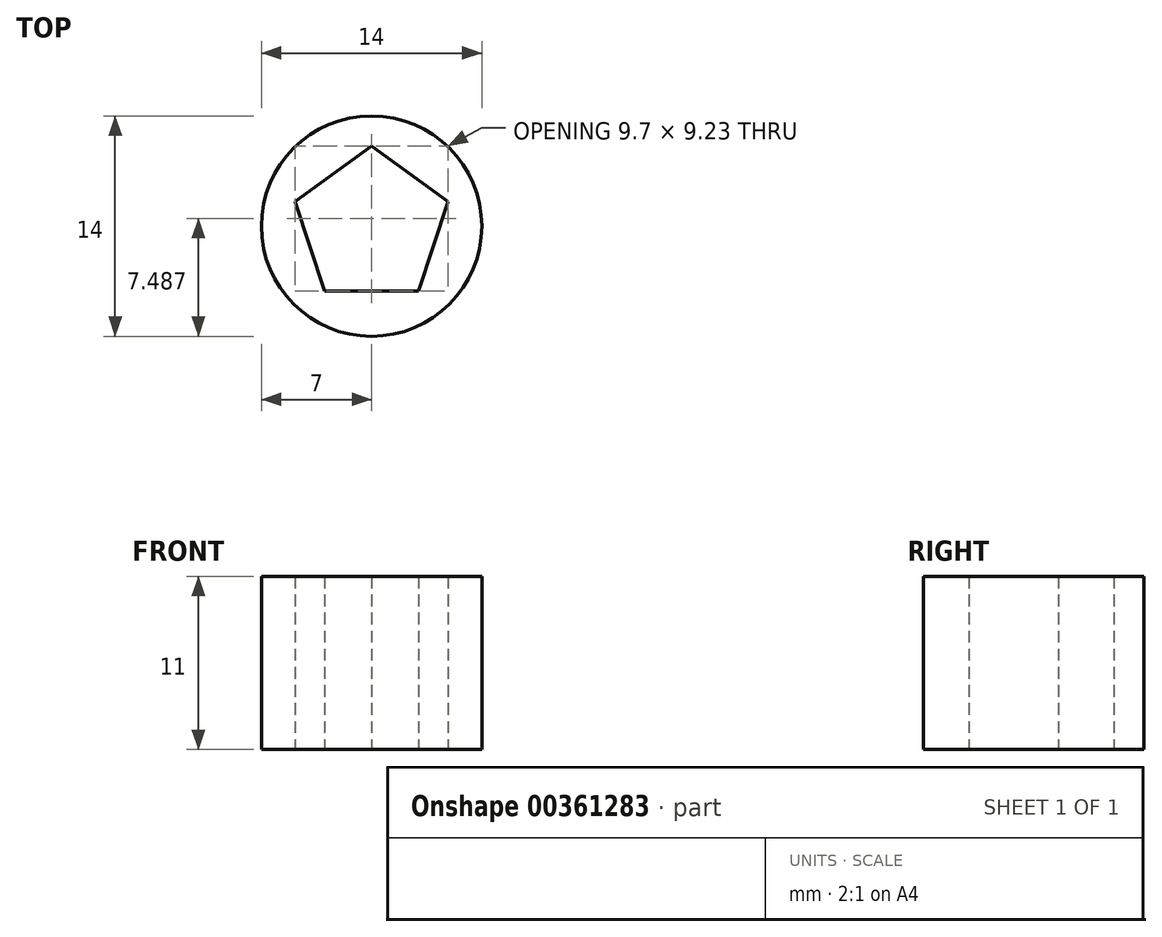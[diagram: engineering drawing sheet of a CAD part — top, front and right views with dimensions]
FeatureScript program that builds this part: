
annotation { "Feature Type Name" : "Feature", "Feature Type Description" : "" }
export const myFeature = defineFeature(function(context is Context, id is Id, definition is map)
    precondition{}
    {
        {
            var Q0;
            Q0=qCreatedBy(makeId("Top.planeOp"),FACE);
            var sketch = newSketch(context, id + "F0", { "sketchPlane" : qUnion([Q0])});
            skCircle(sketch, "E0.cCircle", {"center": v(0, 0) * mm, "radius": 4.13 * mm, "construction": true});
            skLineSegment(sketch, "E0.0", {"start": v(4.85, 1.58) * mm, "end": v(3, -4.13) * mm});
            skLineSegment(sketch, "E0.1", {"start": v(3, -4.13) * mm, "end": v(-3, -4.13) * mm});
            skLineSegment(sketch, "E0.2", {"start": v(-3, -4.13) * mm, "end": v(-4.85, 1.58) * mm});
            skLineSegment(sketch, "E0.3", {"start": v(-4.85, 1.58) * mm, "end": v(0, 5.1) * mm});
            skLineSegment(sketch, "E0.4", {"start": v(0, 5.1) * mm, "end": v(4.85, 1.58) * mm});
            skPoint(sketch, "E0.0.midPoint", {"position": v(3.92, -1.27) * mm});
            skCircle(sketch, "E1", {"center": v(0, 0) * mm, "radius": 7 * mm});
            skSolve(sketch);
        }
        {
            var Q0;
            Q0=makeQuery(id+"F0.imprint","IMPRINT",FACE,{"disambiguationData":[TD([[makeQuery(id+"F0.imprint","IMPRINT",EDGE,{"derivedFrom":sQuery(id+"F0.wireOp",EDGE,"E0.0")}),1.0]])]});
            extrude(context, id + "F1", {"entities" : qUnion([Q0]), "depth" : 11 * mm});
        }
    });
